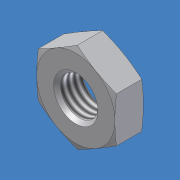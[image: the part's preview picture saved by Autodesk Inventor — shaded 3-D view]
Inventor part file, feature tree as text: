
AUTODESK INVENTOR PART (.ipt)
format: ipt  version: 2012 (Build 160160000, 160)  size: 126,976 bytes
history: native  units: mm (DEFAULTED — no unit token found)
features: other x70, sketch x3, revolve x2, extrude x1, thread x1
ambient origin geometry x8: Origin, YZ Plane, XZ Plane, XY Plane, X Axis, Y Axis, Z Axis, Center Point
bodies: Solid1 (feature_tree)
feature tree (77):
  sketch  "Sketch_8"  dims[d0=360.0deg d1=4.064mm d2=0.0mm]
  sketch  "Sketch_10"  dims[d3=360.0deg d4=3.08102mm d5=0.0mm]
  revolve  "Revolution1"  [1 undecoded]
  extrude  "Extrusion1"  Depth=3.08102mm TaperAngle=0.0deg
  revolve  "Revolution2"  [1 undecoded]
  thread  "Thread1"  [1 undecoded]
  other  "NUT_XY"
  other  "NUT_YZ"
  other  "NUT_ZX"
  other  "NUT_X"
  other  "NUT_Y"
  other  "NUT_Z"
  other  "NUT_Center"
  other  "a1_XY"
  other  "a1_YZ"
  other  "a1_ZX"
  other  "a1_X"
  other  "a1_Y"
  other  "a1_Z"
  other  "a1_Center"
  other  "a2_XY"
  other  "a2_YZ"
  other  "a2_ZX"
  other  "a2_X"
  other  "a2_Y"
  other  "a2_Z"
  other  "a2_Center"
  other  "b1_XY"
  other  "b1_YZ"
  other  "b1_ZX"
  other  "b1_X"
  other  "b1_Y"
  other  "b1_Z"
  other  "b1_Center"
  other  "b2_XY"
  other  "b2_YZ"
  other  "b2_ZX"
  other  "b2_X"
  other  "b2_Y"
  other  "b2_Z"
  other  "b2_Center"
  other  "e_XY"
  other  "e_YZ"
  other  "e_ZX"
  other  "e_X"
  other  "e_Y"
  other  "e_Z"
  other  "e_Center"
  other  "th1_XY"
  other  "th1_YZ"
  other  "th1_ZX"
  other  "th1_X"
  other  "th1_Y"
  other  "th1_Z"
  other  "th1_Center"
  other  "th2_XY"
  other  "th2_YZ"
  other  "th2_ZX"
  other  "th2_X"
  other  "th2_Y"
  other  "th2_Z"
  other  "th2_Center"
  other  "ol1_XY"
  other  "ol1_YZ"
  other  "ol1_ZX"
  other  "ol1_X"
  other  "ol1_Y"
  other  "ol1_Z"
  other  "ol1_Center"
  other  "ol2_XY"
  other  "ol2_YZ"
  other  "ol2_ZX"
  other  "ol2_X"
  other  "ol2_Y"
  other  "ol2_Z"
  other  "ol2_Center"
  sketch  "Sketch_11"
note: 3 required parameter values undecoded (feature->parameter linkage not recoverable at this tier; creation-order binding heuristic only, values carry confidence <= 0.55)